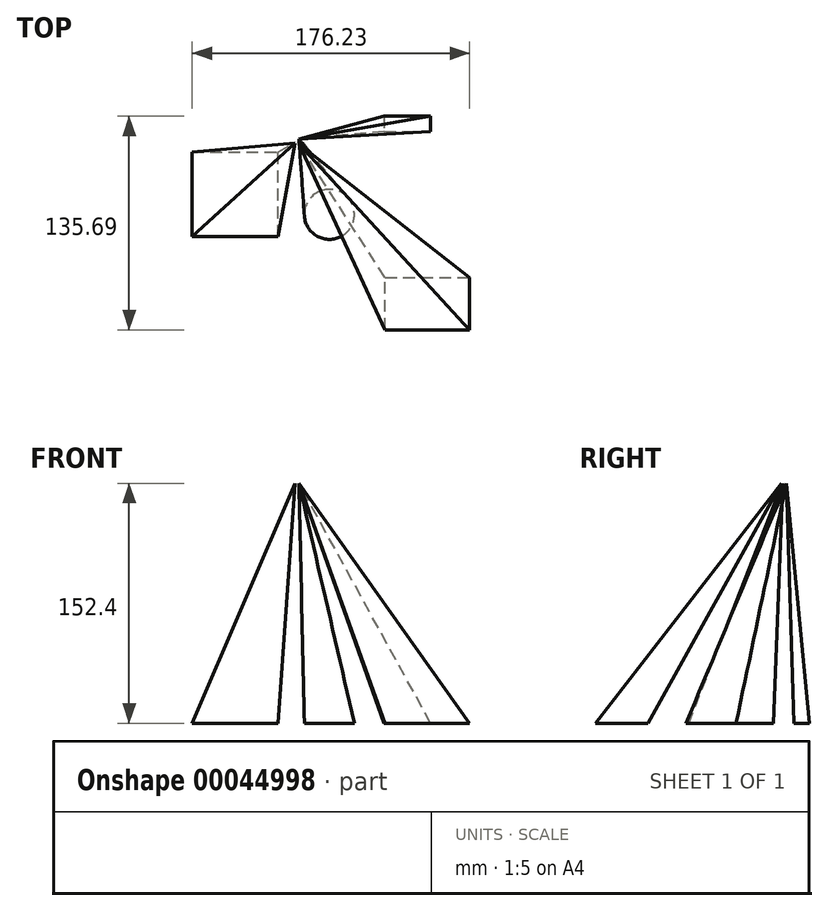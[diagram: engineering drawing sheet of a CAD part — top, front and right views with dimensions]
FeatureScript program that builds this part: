
annotation { "Feature Type Name" : "Feature", "Feature Type Description" : "" }
export const myFeature = defineFeature(function(context is Context, id is Id, definition is map)
    precondition{}
    {
        {
            var Q0;
            Q0=qCreatedBy(makeId("Top.planeOp"),FACE);
            var sketch = newSketch(context, id + "F0", { "sketchPlane" : qUnion([Q0])});
            skLineSegment(sketch, "E0.bottom", {"start": v(-87.12, -14.15) * mm, "end": v(-32.64, -14.15) * mm});
            skLineSegment(sketch, "E0.top", {"start": v(-87.12, 39.76) * mm, "end": v(-32.64, 39.76) * mm});
            skLineSegment(sketch, "E0.left", {"start": v(-87.12, -14.15) * mm, "end": v(-87.12, 39.76) * mm});
            skLineSegment(sketch, "E0.right", {"start": v(-32.64, -14.15) * mm, "end": v(-32.64, 39.76) * mm});
            skLineSegment(sketch, "E1.bottom", {"start": v(34.78, 62.37) * mm, "end": v(64.36, 62.37) * mm});
            skLineSegment(sketch, "E1.top", {"start": v(34.78, 52.7) * mm, "end": v(64.36, 52.7) * mm});
            skLineSegment(sketch, "E1.left", {"start": v(34.78, 62.37) * mm, "end": v(34.78, 52.7) * mm});
            skLineSegment(sketch, "E1.right", {"start": v(64.36, 62.37) * mm, "end": v(64.36, 52.7) * mm});
            skLineSegment(sketch, "E2.bottom", {"start": v(35.35, -73.32) * mm, "end": v(89.11, -73.32) * mm});
            skLineSegment(sketch, "E2.top", {"start": v(35.35, -40.04) * mm, "end": v(89.11, -40.04) * mm});
            skLineSegment(sketch, "E2.left", {"start": v(35.35, -73.32) * mm, "end": v(35.35, -40.04) * mm});
            skLineSegment(sketch, "E2.right", {"start": v(89.11, -73.32) * mm, "end": v(89.11, -40.04) * mm});
            skCircle(sketch, "E3", {"center": v(0, 0) * mm, "radius": 15.9 * mm});
            skSolve(sketch);
        }
        {
            var Q0;
            Q0=qCreatedBy(makeId("Top.planeOp"),FACE);
            cPlane(context, id + "F1", {"entities" : qUnion([Q0]), "cplaneType" : CPlaneType.OFFSET, "offset" : 152.4 * mm, "width" : 152.4 * mm, "height" : 152.4 * mm});
        }
        {
            var Q0;
            Q0=qCreatedBy(id+"F1.planeOp",FACE);
            var sketch = newSketch(context, id + "F2", { "sketchPlane" : qUnion([Q0])});
            skPoint(sketch, "E4", {"position": v(-19.3, 44.54) * mm});
            skPoint(sketch, "E5", {"position": v(-17.65, 44.54) * mm});
            skPoint(sketch, "E6", {"position": v(-19.5, 42.74) * mm});
            skPoint(sketch, "E7", {"position": v(-19.3, 47.86) * mm});
            skPoint(sketch, "E8", {"position": v(-21.92, 45.45) * mm});
            skSolve(sketch);
        }
        {
            var Q0;
            Q0=makeQuery(id+"F0.imprint","IMPRINT",FACE,{"disambiguationData":[TD([[makeQuery(id+"F0.imprint","IMPRINT",EDGE,{"derivedFrom":sQuery(id+"F0.wireOp",EDGE,"E2.bottom")}),1.0]])]});
            var Q1;
            Q1=sQuery(id+"F2.wireOp",VERTEX,"E4");
            loft(context, id + "F3", {"sheetProfilesArray" : [{ "sheetProfileEntities" : qUnion([Q0]) }, { "sheetProfileEntities" : qUnion([Q1]) }]});
        }
        {
            var Q0;
            Q0=makeQuery(id+"F0.imprint","IMPRINT",FACE,{"disambiguationData":[TD([[makeQuery(id+"F0.imprint","IMPRINT",EDGE,{"derivedFrom":sQuery(id+"F0.wireOp",EDGE,"E0.bottom")}),1.0]])]});
            var Q1;
            Q1=sQuery(id+"F2.wireOp",VERTEX,"E8");
            loft(context, id + "F4", {"sheetProfilesArray" : [{ "sheetProfileEntities" : qUnion([Q0]) }, { "sheetProfileEntities" : qUnion([Q1]) }]});
        }
        {
            var Q0;
            Q0=makeQuery(id+"F0.imprint","IMPRINT",FACE,{"disambiguationData":[TD([[makeQuery(id+"F0.imprint","IMPRINT",EDGE,{"derivedFrom":sQuery(id+"F0.wireOp",EDGE,"E3")}),1.0]])]});
            var Q1;
            Q1=sQuery(id+"F2.wireOp",VERTEX,"E7");
            loft(context, id + "F5", {"sheetProfilesArray" : [{ "sheetProfileEntities" : qUnion([Q0]) }, { "sheetProfileEntities" : qUnion([Q1]) }]});
        }
        {
            var Q0;
            Q0=makeQuery(id+"F0.imprint","IMPRINT",FACE,{"disambiguationData":[TD([[makeQuery(id+"F0.imprint","IMPRINT",EDGE,{"derivedFrom":sQuery(id+"F0.wireOp",EDGE,"E1.bottom")}),-1.0]])]});
            var Q1;
            Q1=sQuery(id+"F2.wireOp",VERTEX,"E7");
            loft(context, id + "F6", {"sheetProfilesArray" : [{ "sheetProfileEntities" : qUnion([Q0]) }, { "sheetProfileEntities" : qUnion([Q1]) }]});
        }
    });
